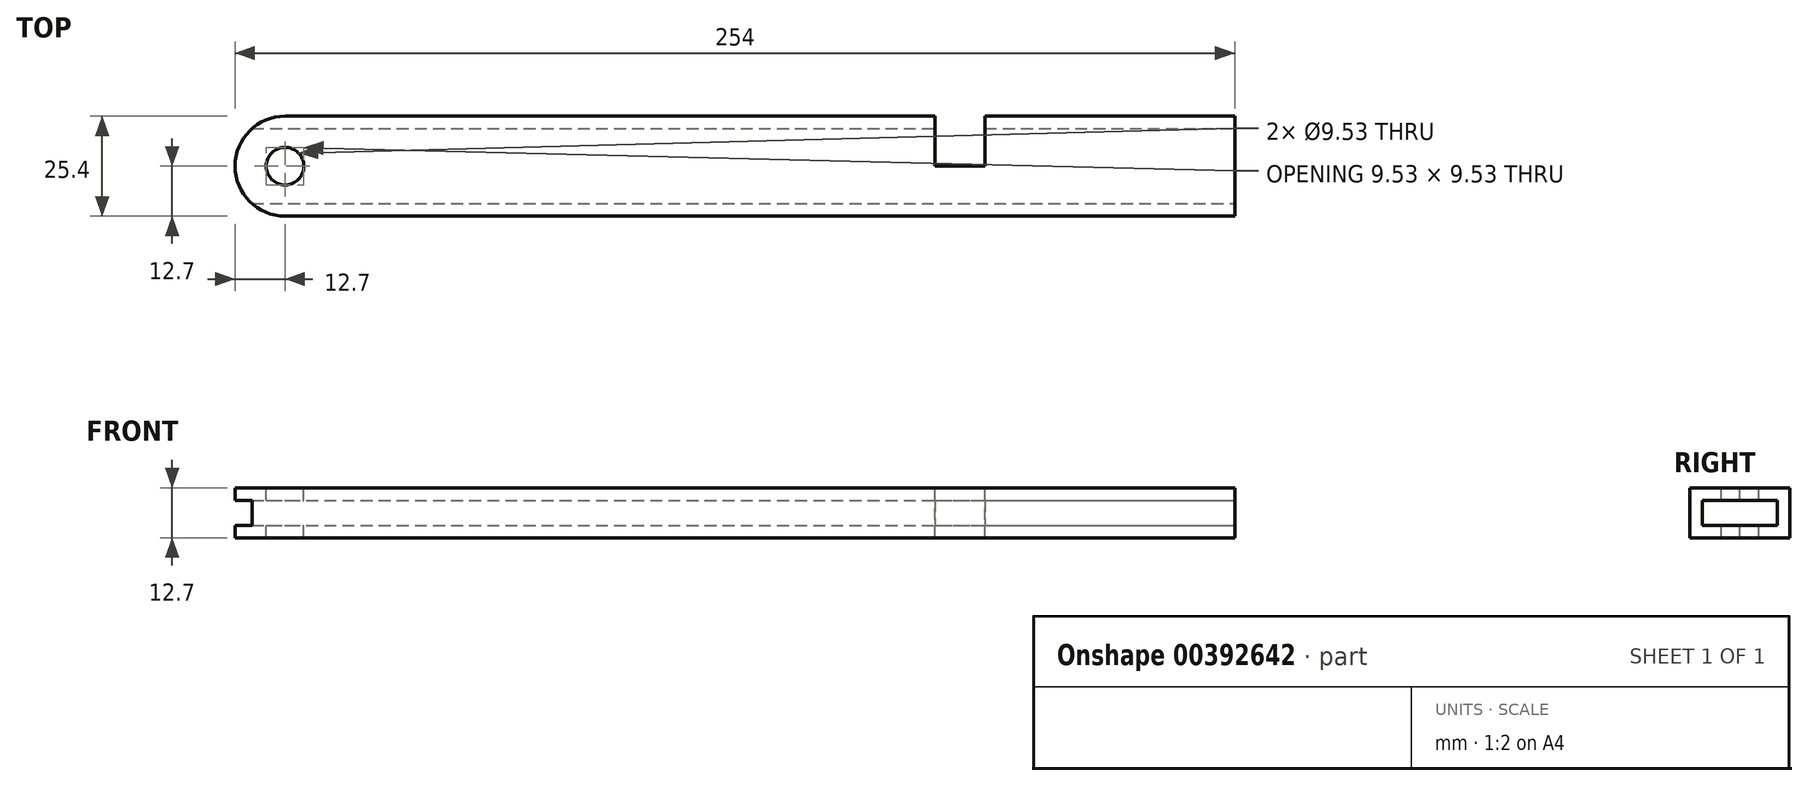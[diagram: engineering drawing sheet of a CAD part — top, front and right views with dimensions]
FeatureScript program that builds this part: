
annotation { "Feature Type Name" : "Feature", "Feature Type Description" : "" }
export const myFeature = defineFeature(function(context is Context, id is Id, definition is map)
    precondition{}
    {
        {
            var Q0;
            Q0=qCreatedBy(makeId("Top.planeOp"),FACE);
            var sketch = newSketch(context, id + "F0", { "sketchPlane" : qUnion([Q0])});
            skLineSegment(sketch, "E0.bottom", {"start": v(-127, 12.7) * mm, "end": v(127, 12.7) * mm});
            skLineSegment(sketch, "E0.top", {"start": v(-127, -12.7) * mm, "end": v(127, -12.7) * mm});
            skLineSegment(sketch, "E0.left", {"start": v(-127, 12.7) * mm, "end": v(-127, -12.7) * mm});
            skLineSegment(sketch, "E0.right", {"start": v(127, 12.7) * mm, "end": v(127, -12.7) * mm});
            skPoint(sketch, "E0.middle", {"position": v(0, 0) * mm});
            skSolve(sketch);
        }
        {
            var Q0;
            Q0 = qSketchRegion(id + "F0", true);
            extrude(context, id + "F1", {"entities" : qUnion([Q0]), "endBound" : BoundingType.SYMMETRIC, "depth" : 12.7 * mm});
        }
        {
            var Q0;
            Q0=makeQuery(id+"F1.opExtrude","SWEPT_EDGE",EDGE,{"disambiguationData":[OSD([sQuery(id+"F0.wireOp",EDGE,"E0.bottom"),sQuery(id+"F0.wireOp",EDGE,"E0.left")])]});
            var Q1;
            Q1=makeQuery(id+"F1.opExtrude","SWEPT_EDGE",EDGE,{"disambiguationData":[OSD([sQuery(id+"F0.wireOp",EDGE,"E0.top"),sQuery(id+"F0.wireOp",EDGE,"E0.left")])]});
            fillet(context, id + "F2", {"entities" : qUnion([Q0, Q1]), "radius" : 12.7 * mm, "tangentPropagation" : true, "allowEdgeOverflow" : false});
        }
        {
            var Q0;
            Q0=makeQuery(id+"F1.opExtrude","CAP_FACE",FACE,{"disambiguationData":[OSD([sQuery(id+"F0.wireOp",EDGE,"E0.bottom"),sQuery(id+"F0.wireOp",EDGE,"E0.top"),sQuery(id+"F0.wireOp",EDGE,"E0.left"),sQuery(id+"F0.wireOp",EDGE,"E0.right")])],"isStart":false});
            var sketch = newSketch(context, id + "F3", { "sketchPlane" : qUnion([Q0])});
            skCircle(sketch, "E1", {"center": v(-114.3, 0) * mm, "radius": 4.76 * mm});
            skSolve(sketch);
        }
        {
            var Q0;
            Q0 = qSketchRegion(id + "F3", true);
            extrude(context, id + "F4", {"entities" : qUnion([Q0]), "operationType" : NewBodyOperationType.REMOVE, "endBound" : BoundingType.THROUGH_ALL, "oppositeDirection" : true, "depth" : 25.4 * mm});
        }
        {
            var Q0;
            Q0=qCreatedBy(makeId("Right.planeOp"),FACE);
            var sketch = newSketch(context, id + "F5", { "sketchPlane" : qUnion([Q0])});
            skLineSegment(sketch, "E2.bottom", {"start": v(-9.53, 3.18) * mm, "end": v(9.53, 3.18) * mm});
            skLineSegment(sketch, "E2.top", {"start": v(-9.52, -3.18) * mm, "end": v(9.52, -3.18) * mm});
            skLineSegment(sketch, "E2.left", {"start": v(-9.53, 3.18) * mm, "end": v(-9.53, -3.17) * mm});
            skLineSegment(sketch, "E2.right", {"start": v(9.53, 3.18) * mm, "end": v(9.53, -3.17) * mm});
            skPoint(sketch, "E2.middle", {"position": v(0, 0) * mm});
            skSolve(sketch);
        }
        {
            var Q0;
            Q0 = qSketchRegion(id + "F5", true);
            extrude(context, id + "F6", {"entities" : qUnion([Q0]), "operationType" : NewBodyOperationType.REMOVE, "endBound" : BoundingType.THROUGH_ALL, "oppositeDirection" : true, "depth" : 25.4 * mm, "hasSecondDirection" : true, "secondDirectionBound" : SecondDirectionBoundingType.THROUGH_ALL, "secondDirectionOppositeDirection" : false, "secondDirectionDepth" : 25.4 * mm});
        }
        {
            var Q0;
            Q0=makeQuery(id+"F1.opExtrude","CAP_FACE",FACE,{"disambiguationData":[OSD([sQuery(id+"F0.wireOp",EDGE,"E0.bottom"),sQuery(id+"F0.wireOp",EDGE,"E0.top"),sQuery(id+"F0.wireOp",EDGE,"E0.left"),sQuery(id+"F0.wireOp",EDGE,"E0.right")])],"isStart":false});
            var sketch = newSketch(context, id + "F7", { "sketchPlane" : qUnion([Q0])});
            skLineSegment(sketch, "E3.bottom", {"start": v(63.5, 12.7) * mm, "end": v(50.8, 12.7) * mm});
            skLineSegment(sketch, "E3.top", {"start": v(63.5, 0) * mm, "end": v(50.8, 0) * mm});
            skLineSegment(sketch, "E3.left", {"start": v(63.5, 12.7) * mm, "end": v(63.5, 0) * mm});
            skLineSegment(sketch, "E3.right", {"start": v(50.8, 12.7) * mm, "end": v(50.8, 0) * mm});
            skSolve(sketch);
        }
        {
            var Q0;
            Q0 = qSketchRegion(id + "F7", true);
            extrude(context, id + "F8", {"entities" : qUnion([Q0]), "operationType" : NewBodyOperationType.REMOVE, "endBound" : BoundingType.THROUGH_ALL, "oppositeDirection" : true, "depth" : 25.4 * mm});
        }
    });
